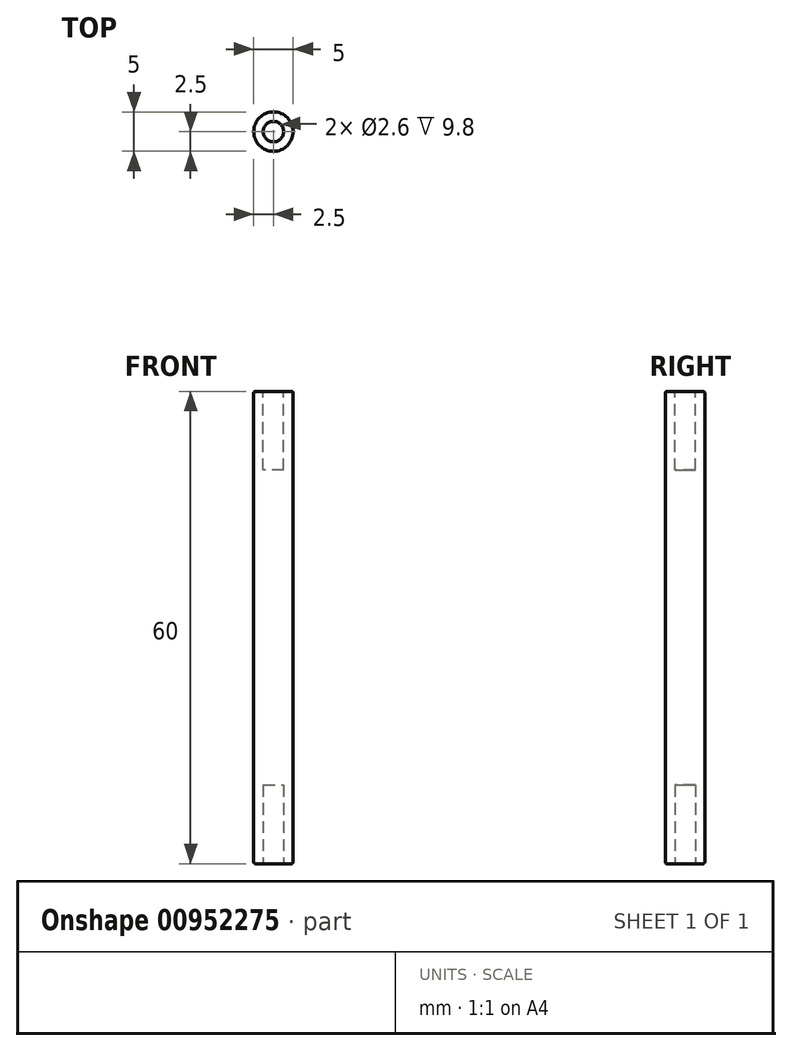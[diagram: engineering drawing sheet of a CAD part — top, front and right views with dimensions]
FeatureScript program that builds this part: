
annotation { "Feature Type Name" : "Feature", "Feature Type Description" : "" }
export const myFeature = defineFeature(function(context is Context, id is Id, definition is map)
    precondition{}
    {
        {
            var Q0;
            Q0=qCreatedBy(makeId("Top.planeOp"),FACE);
            var sketch = newSketch(context, id + "F0", { "sketchPlane" : qUnion([Q0])});
            skCircle(sketch, "E0", {"center": v(0, 0) * mm, "radius": 2.5 * mm});
            skSolve(sketch);
        }
        {
            var Q0;
            Q0 = qSketchRegion(id + "F0", true);
            extrude(context, id + "F1", {"entities" : qUnion([Q0]), "depth" : 60 * mm, "offsetDistance" : 25 * mm, "symmetric" : true});
        }
        {
            var Q0;
            Q0=makeQuery(id+"F1.opExtrude","CAP_FACE",FACE,{"disambiguationData":[OSD([sQuery(id+"F0.wireOp",EDGE,"E0")])],"isStart":false});
            var sketch = newSketch(context, id + "F2", { "sketchPlane" : qUnion([Q0])});
            skCircle(sketch, "E1", {"center": v(0, 0) * mm, "radius": 1.3 * mm});
            skSolve(sketch);
        }
        {
            var Q0;
            Q0 = qSketchRegion(id + "F2", true);
            extrude(context, id + "F3", {"entities" : qUnion([Q0]), "operationType" : NewBodyOperationType.REMOVE, "oppositeDirection" : true, "depth" : 10 * mm, "offsetDistance" : 25 * mm});
        }
        {
            var Q0;
            Q0=makeQuery(id+"F1.opExtrude","CAP_FACE",FACE,{"disambiguationData":[OSD([sQuery(id+"F0.wireOp",EDGE,"E0")])],"isStart":true});
            var sketch = newSketch(context, id + "F4", { "sketchPlane" : qUnion([Q0])});
            skCircle(sketch, "E2", {"center": v(0, 0) * mm, "radius": 1.3 * mm});
            skSolve(sketch);
        }
        {
            var Q0;
            Q0 = qSketchRegion(id + "F4", true);
            extrude(context, id + "F5", {"entities" : qUnion([Q0]), "operationType" : NewBodyOperationType.REMOVE, "oppositeDirection" : true, "depth" : 10 * mm, "offsetDistance" : 25 * mm});
        }
        {
            var Q0;
            Q0=makeQuery(id+"F1.opExtrude","CAP_FACE",FACE,{"disambiguationData":[OSD([sQuery(id+"F0.wireOp",EDGE,"E0")])],"isStart":true});
            var Q1;
            Q1=makeQuery(id+"F1.opExtrude","CAP_FACE",FACE,{"disambiguationData":[OSD([sQuery(id+"F0.wireOp",EDGE,"E0")])],"isStart":false});
            fillet(context, id + "F6", {"entities" : qUnion([Q0, Q1]), "tangentPropagation" : true, "radius" : 0.2 * mm, "defaultsChanged" : false, "vertexSettings" : [], "allowEdgeOverflow" : false});
        }
    });
